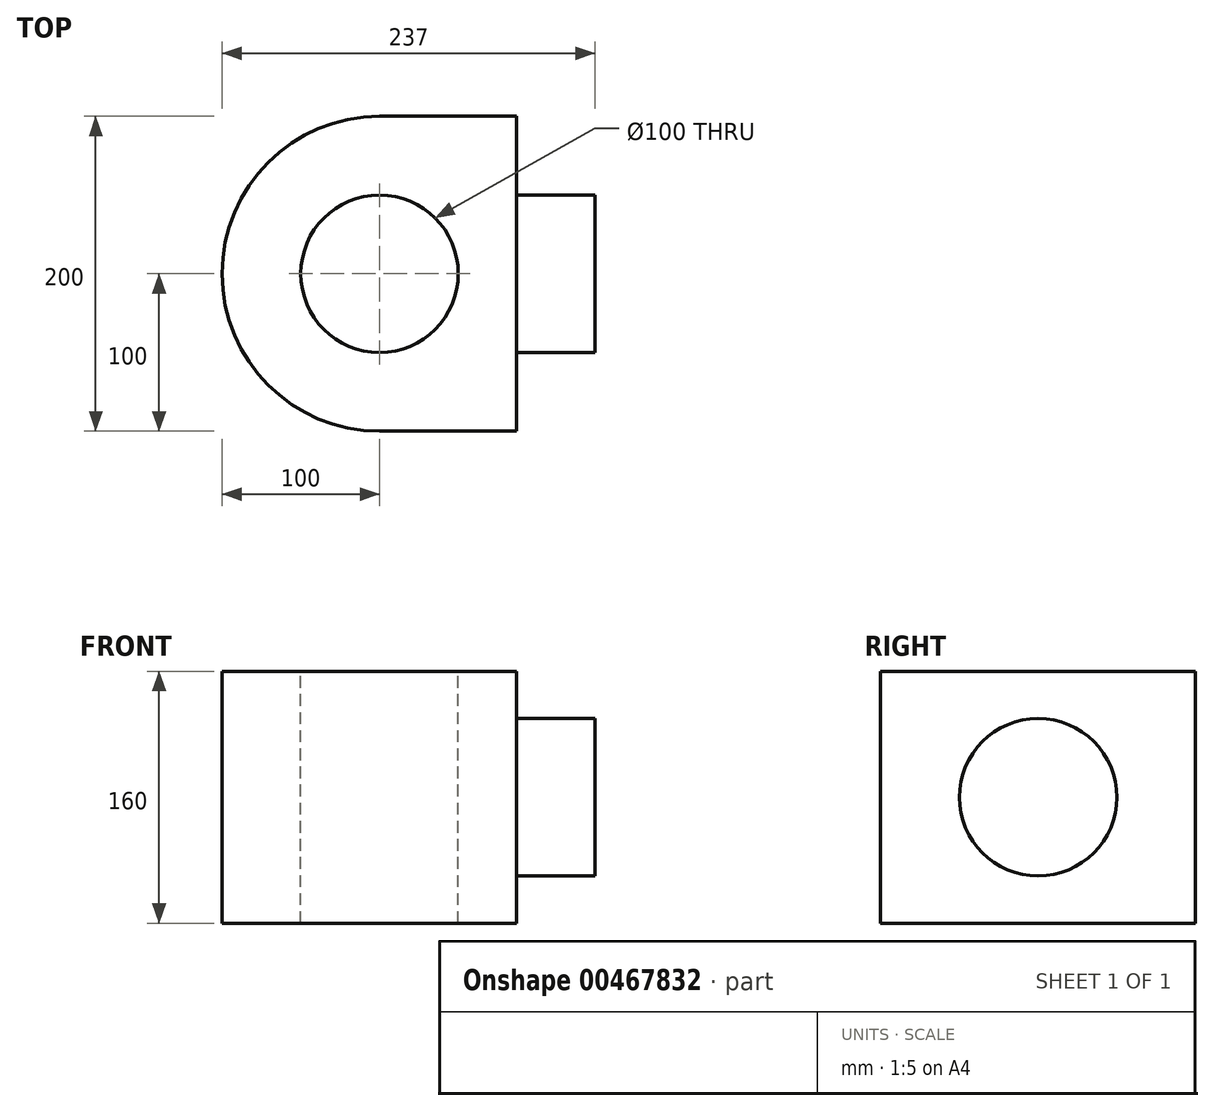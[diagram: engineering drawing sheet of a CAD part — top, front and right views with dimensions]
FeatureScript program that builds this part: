
annotation { "Feature Type Name" : "Feature", "Feature Type Description" : "" }
export const myFeature = defineFeature(function(context is Context, id is Id, definition is map)
    precondition{}
    {
        {
            var Q0;
            Q0=qCreatedBy(makeId("Top.planeOp"),FACE);
            var sketch = newSketch(context, id + "F0", { "sketchPlane" : qUnion([Q0])});
            skLineSegment(sketch, "E0.bottom", {"start": v(43.5, -100) * mm, "end": v(-43.5, -100) * mm});
            skLineSegment(sketch, "E0.top", {"start": v(43.5, 100) * mm, "end": v(-43.5, 100) * mm});
            skLineSegment(sketch, "E0.left", {"start": v(43.5, -100) * mm, "end": v(43.5, 100) * mm});
            skPoint(sketch, "E0.middle", {"position": v(0, 0) * mm});
            skArc(sketch, "E1", {"start": v(-43.5, 100) * mm, "mid": v(-143.5, 0) * mm, "end": v(-43.5, -100) * mm});
            skSolve(sketch);
        }
        {
            var Q0;
            Q0 = qSketchRegion(id + "F0", true);
            extrude(context, id + "F1", {"entities" : qUnion([Q0]), "depth" : 160 * mm});
        }
        {
            var Q0;
            Q0=makeQuery(id+"F1.opExtrude","CAP_FACE",FACE,{"disambiguationData":[OSD([sQuery(id+"F0.wireOp",EDGE,"E0.bottom"),sQuery(id+"F0.wireOp",EDGE,"E0.top"),sQuery(id+"F0.wireOp",EDGE,"E0.left"),sQuery(id+"F0.wireOp",EDGE,"E1")])],"isStart":false});
            var sketch = newSketch(context, id + "F2", { "sketchPlane" : qUnion([Q0])});
            skCircle(sketch, "E2", {"center": v(-43.5, 0) * mm, "radius": 50 * mm});
            skSolve(sketch);
        }
        {
            var Q0;
            Q0=makeQuery(id+"F2.imprint","IMPRINT",FACE,{"disambiguationData":[TD([[makeQuery(id+"F2.imprint","IMPRINT",EDGE,{"derivedFrom":sQuery(id+"F2.wireOp",EDGE,"E2")}),1.0]])]});
            extrude(context, id + "F3", {"entities" : qUnion([Q0]), "operationType" : NewBodyOperationType.REMOVE, "oppositeDirection" : true, "depth" : 504 * mm, "offsetDistance" : 25 * mm});
        }
        {
            var Q0;
            Q0=makeQuery(id+"F1.opExtrude","SWEPT_FACE",FACE,{"disambiguationData":[OSD([sQuery(id+"F0.wireOp",EDGE,"E0.left")])]});
            var sketch = newSketch(context, id + "F4", { "sketchPlane" : qUnion([Q0])});
            skCircle(sketch, "E3", {"center": v(0, 80) * mm, "radius": 50 * mm});
            skPoint(sketch, "E3.centerSnap0", {"position": v(100, 80) * mm});
            skSolve(sketch);
        }
        {
            var Q0;
            Q0=makeQuery(id+"F4.imprint","IMPRINT",FACE,{"disambiguationData":[TD([[makeQuery(id+"F4.imprint","IMPRINT",EDGE,{"derivedFrom":sQuery(id+"F4.wireOp",EDGE,"E3")}),1.0]])]});
            extrude(context, id + "F5", {"entities" : qUnion([Q0]), "operationType" : NewBodyOperationType.ADD, "depth" : 50 * mm, "offsetDistance" : 25 * mm});
        }
    });
